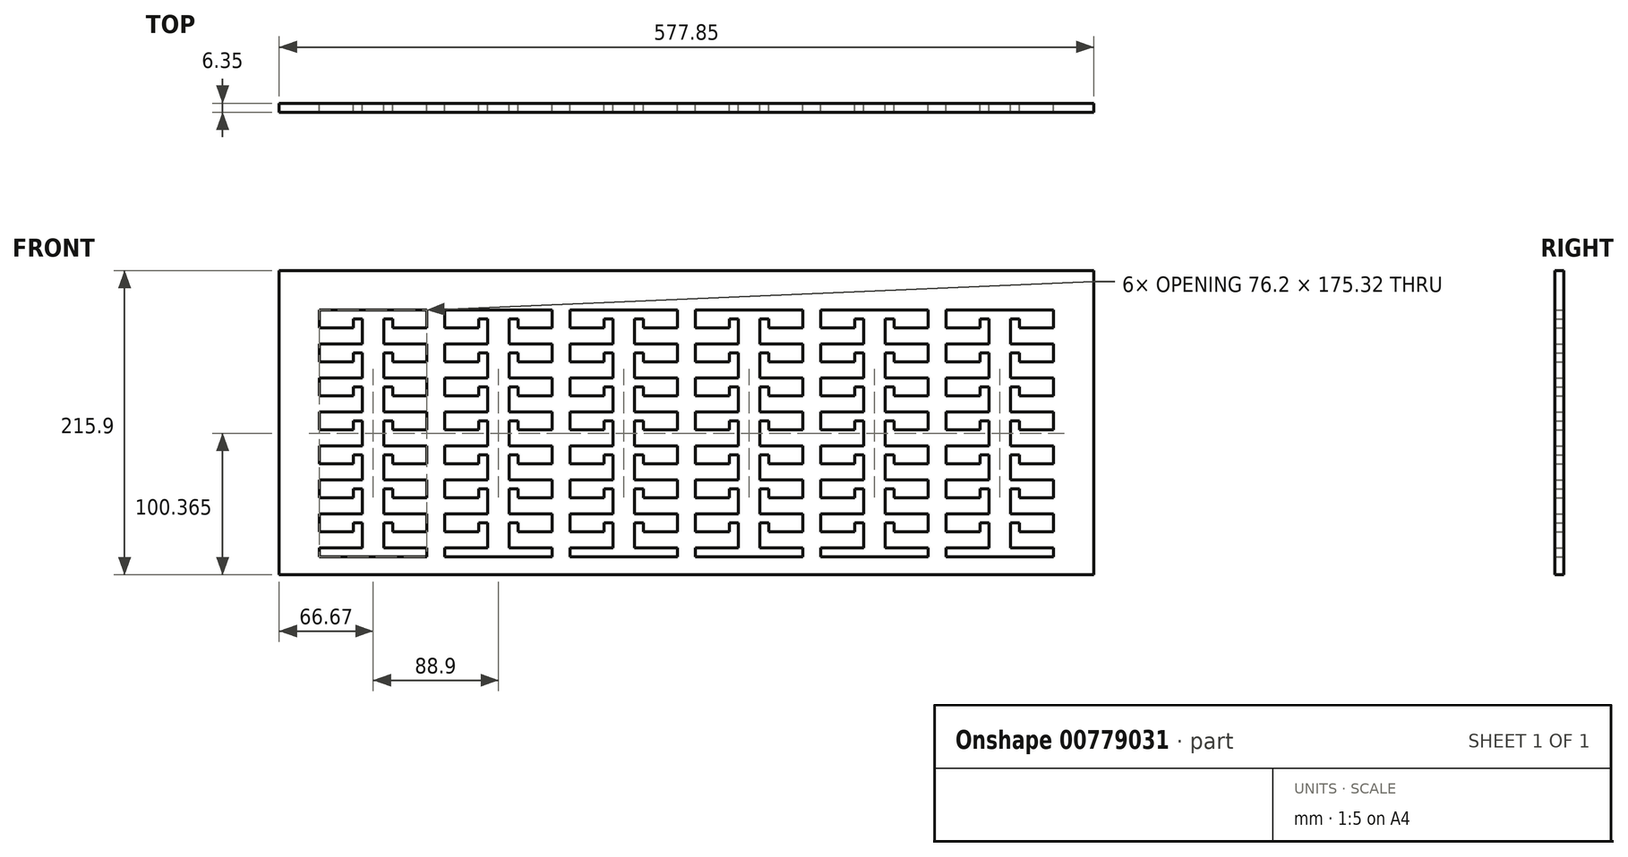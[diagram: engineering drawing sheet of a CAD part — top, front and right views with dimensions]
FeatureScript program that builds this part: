
annotation { "Feature Type Name" : "Feature", "Feature Type Description" : "" }
export const myFeature = defineFeature(function(context is Context, id is Id, definition is map)
    precondition{}
    {
        {
            var Q0;
            Q0=qCreatedBy(makeId("Front.planeOp"),FACE);
            var sketch = newSketch(context, id + "F0", { "sketchPlane" : qUnion([Q0])});
            skLineSegment(sketch, "E0", {"start": v(-97.96, -49.5) * mm, "end": v(-67.48, -49.5) * mm});
            skLineSegment(sketch, "E1", {"start": v(-67.48, -49.5) * mm, "end": v(-67.48, -31.72) * mm});
            skLineSegment(sketch, "E2", {"start": v(-67.48, -31.72) * mm, "end": v(-73.83, -31.72) * mm});
            skLineSegment(sketch, "E3", {"start": v(-73.83, -31.72) * mm, "end": v(-73.83, -38.07) * mm});
            skLineSegment(sketch, "E4", {"start": v(-73.83, -38.07) * mm, "end": v(-97.96, -38.07) * mm});
            skLineSegment(sketch, "E5", {"start": v(-97.96, -38.07) * mm, "end": v(-97.96, -25.37) * mm});
            skLineSegment(sketch, "E6", {"start": v(-97.96, -25.37) * mm, "end": v(-67.48, -25.37) * mm});
            skLineSegment(sketch, "E7", {"start": v(-67.48, -25.37) * mm, "end": v(-67.48, -7.6) * mm});
            skLineSegment(sketch, "E8", {"start": v(-67.48, -7.6) * mm, "end": v(-73.83, -7.6) * mm});
            skLineSegment(sketch, "E9", {"start": v(-73.83, -7.6) * mm, "end": v(-73.83, -13.94) * mm});
            skLineSegment(sketch, "E10", {"start": v(-73.83, -13.94) * mm, "end": v(-97.96, -13.94) * mm});
            skLineSegment(sketch, "E11", {"start": v(-97.96, -13.94) * mm, "end": v(-97.96, -1.24) * mm});
            skLineSegment(sketch, "E12", {"start": v(-97.96, -1.24) * mm, "end": v(-67.48, -1.24) * mm});
            skLineSegment(sketch, "E13", {"start": v(-67.48, -1.24) * mm, "end": v(-67.48, 16.54) * mm});
            skLineSegment(sketch, "E14", {"start": v(-67.48, 16.54) * mm, "end": v(-73.83, 16.54) * mm});
            skLineSegment(sketch, "E15", {"start": v(-73.83, 16.54) * mm, "end": v(-73.83, 10.19) * mm});
            skLineSegment(sketch, "E16", {"start": v(-73.83, 10.19) * mm, "end": v(-97.96, 10.19) * mm});
            skLineSegment(sketch, "E17", {"start": v(-97.96, 10.19) * mm, "end": v(-97.96, 22.89) * mm});
            skLineSegment(sketch, "E18", {"start": v(-97.96, 22.89) * mm, "end": v(-67.48, 22.89) * mm});
            skLineSegment(sketch, "E19", {"start": v(-67.48, 22.89) * mm, "end": v(-67.48, 40.67) * mm});
            skLineSegment(sketch, "E20", {"start": v(-67.48, 40.67) * mm, "end": v(-73.83, 40.67) * mm});
            skLineSegment(sketch, "E21", {"start": v(-73.83, 40.67) * mm, "end": v(-73.83, 34.32) * mm});
            skLineSegment(sketch, "E22", {"start": v(-73.83, 34.32) * mm, "end": v(-97.96, 34.32) * mm});
            skLineSegment(sketch, "E23", {"start": v(-97.96, 34.32) * mm, "end": v(-97.96, 47.02) * mm});
            skLineSegment(sketch, "E24", {"start": v(-21.76, -80.05) * mm, "end": v(-21.76, -73.63) * mm});
            skLineSegment(sketch, "E25", {"start": v(-21.76, -73.63) * mm, "end": v(-52.24, -73.63) * mm});
            skLineSegment(sketch, "E26", {"start": v(-52.24, -73.63) * mm, "end": v(-52.24, -55.85) * mm});
            skLineSegment(sketch, "E27", {"start": v(-52.24, -55.85) * mm, "end": v(-45.89, -55.85) * mm});
            skLineSegment(sketch, "E28", {"start": v(-45.89, -55.85) * mm, "end": v(-45.89, -62.2) * mm});
            skLineSegment(sketch, "E29", {"start": v(-45.89, -62.2) * mm, "end": v(-21.76, -62.2) * mm});
            skLineSegment(sketch, "E30", {"start": v(-21.76, -62.2) * mm, "end": v(-21.76, -49.5) * mm});
            skLineSegment(sketch, "E31", {"start": v(-21.76, -49.5) * mm, "end": v(-52.24, -49.5) * mm});
            skLineSegment(sketch, "E32", {"start": v(-52.24, -49.5) * mm, "end": v(-52.24, -31.72) * mm});
            skLineSegment(sketch, "E33", {"start": v(-52.24, -31.72) * mm, "end": v(-45.89, -31.72) * mm});
            skLineSegment(sketch, "E34", {"start": v(-45.89, -31.72) * mm, "end": v(-45.89, -38.07) * mm});
            skLineSegment(sketch, "E35", {"start": v(-45.89, -38.07) * mm, "end": v(-21.76, -38.07) * mm});
            skLineSegment(sketch, "E36", {"start": v(-21.76, -38.07) * mm, "end": v(-21.76, -25.37) * mm});
            skLineSegment(sketch, "E37", {"start": v(-21.76, -25.37) * mm, "end": v(-52.24, -25.37) * mm});
            skLineSegment(sketch, "E38", {"start": v(-52.24, -25.37) * mm, "end": v(-52.24, -7.6) * mm});
            skLineSegment(sketch, "E39", {"start": v(-52.24, -7.6) * mm, "end": v(-45.89, -7.6) * mm});
            skLineSegment(sketch, "E40", {"start": v(-45.89, -7.6) * mm, "end": v(-45.89, -13.94) * mm});
            skLineSegment(sketch, "E41", {"start": v(-45.89, -13.94) * mm, "end": v(-21.76, -13.94) * mm});
            skLineSegment(sketch, "E42", {"start": v(-21.76, -13.94) * mm, "end": v(-21.76, -1.24) * mm});
            skLineSegment(sketch, "E43", {"start": v(-21.76, -1.24) * mm, "end": v(-52.24, -1.24) * mm});
            skLineSegment(sketch, "E44", {"start": v(-52.24, -1.24) * mm, "end": v(-52.24, 16.54) * mm});
            skLineSegment(sketch, "E45", {"start": v(-52.24, 16.54) * mm, "end": v(-45.89, 16.54) * mm});
            skLineSegment(sketch, "E46", {"start": v(-45.89, 16.54) * mm, "end": v(-45.89, 10.19) * mm});
            skLineSegment(sketch, "E47", {"start": v(-45.89, 10.19) * mm, "end": v(-21.76, 10.19) * mm});
            skLineSegment(sketch, "E48", {"start": v(-21.76, 10.19) * mm, "end": v(-21.76, 22.89) * mm});
            skLineSegment(sketch, "E49", {"start": v(-21.76, 22.89) * mm, "end": v(-52.24, 22.89) * mm});
            skLineSegment(sketch, "E50", {"start": v(-52.24, 22.89) * mm, "end": v(-52.24, 40.67) * mm});
            skLineSegment(sketch, "E51", {"start": v(-52.24, 40.67) * mm, "end": v(-45.89, 40.67) * mm});
            skLineSegment(sketch, "E52", {"start": v(-45.89, 40.67) * mm, "end": v(-45.89, 34.32) * mm});
            skLineSegment(sketch, "E53", {"start": v(-45.89, 34.32) * mm, "end": v(-21.76, 34.32) * mm});
            skLineSegment(sketch, "E54", {"start": v(-21.76, 34.32) * mm, "end": v(-21.76, 47.02) * mm});
            skLineSegment(sketch, "E55", {"start": v(-67.48, -73.63) * mm, "end": v(-67.48, -55.85) * mm});
            skLineSegment(sketch, "E56", {"start": v(-73.83, -62.2) * mm, "end": v(-73.83, -55.85) * mm});
            skLineSegment(sketch, "E57", {"start": v(-73.83, -55.85) * mm, "end": v(-67.48, -55.85) * mm});
            skLineSegment(sketch, "E58", {"start": v(-67.48, -73.63) * mm, "end": v(-97.96, -73.63) * mm});
            skLineSegment(sketch, "E59", {"start": v(-97.96, -62.2) * mm, "end": v(-97.96, -49.5) * mm});
            skLineSegment(sketch, "E60", {"start": v(-97.96, -73.63) * mm, "end": v(-97.96, -80.05) * mm});
            skLineSegment(sketch, "E61", {"start": v(-97.96, -62.2) * mm, "end": v(-73.83, -62.2) * mm});
            skLineSegment(sketch, "E62", {"start": v(-97.96, -80.05) * mm, "end": v(-21.76, -80.05) * mm});
            skPoint(sketch, "E63", {"position": v(-59.86, -80.05) * mm});
            skLineSegment(sketch, "E64", {"start": v(-186.86, -49.5) * mm, "end": v(-156.38, -49.5) * mm});
            skLineSegment(sketch, "E65", {"start": v(-156.38, -49.5) * mm, "end": v(-156.38, -31.72) * mm});
            skLineSegment(sketch, "E66", {"start": v(-156.38, -31.72) * mm, "end": v(-162.73, -31.72) * mm});
            skLineSegment(sketch, "E67", {"start": v(-162.73, -31.72) * mm, "end": v(-162.73, -38.07) * mm});
            skLineSegment(sketch, "E68", {"start": v(-162.73, -38.07) * mm, "end": v(-186.86, -38.07) * mm});
            skLineSegment(sketch, "E69", {"start": v(-186.86, -38.07) * mm, "end": v(-186.86, -25.37) * mm});
            skLineSegment(sketch, "E70", {"start": v(-186.86, -25.37) * mm, "end": v(-156.38, -25.37) * mm});
            skLineSegment(sketch, "E71", {"start": v(-156.38, -25.37) * mm, "end": v(-156.38, -7.6) * mm});
            skLineSegment(sketch, "E72", {"start": v(-156.38, -7.6) * mm, "end": v(-162.73, -7.6) * mm});
            skLineSegment(sketch, "E73", {"start": v(-162.73, -7.6) * mm, "end": v(-162.73, -13.94) * mm});
            skLineSegment(sketch, "E74", {"start": v(-162.73, -13.94) * mm, "end": v(-186.86, -13.94) * mm});
            skLineSegment(sketch, "E75", {"start": v(-186.86, -13.94) * mm, "end": v(-186.86, -1.24) * mm});
            skLineSegment(sketch, "E76", {"start": v(-186.86, -1.24) * mm, "end": v(-156.38, -1.24) * mm});
            skLineSegment(sketch, "E77", {"start": v(-156.38, -1.24) * mm, "end": v(-156.38, 16.54) * mm});
            skLineSegment(sketch, "E78", {"start": v(-156.38, 16.54) * mm, "end": v(-162.73, 16.54) * mm});
            skLineSegment(sketch, "E79", {"start": v(-162.73, 16.54) * mm, "end": v(-162.73, 10.19) * mm});
            skLineSegment(sketch, "E80", {"start": v(-162.73, 10.19) * mm, "end": v(-186.86, 10.19) * mm});
            skLineSegment(sketch, "E81", {"start": v(-186.86, 10.19) * mm, "end": v(-186.86, 22.89) * mm});
            skLineSegment(sketch, "E82", {"start": v(-186.86, 22.89) * mm, "end": v(-156.38, 22.89) * mm});
            skLineSegment(sketch, "E83", {"start": v(-156.38, 22.89) * mm, "end": v(-156.38, 40.67) * mm});
            skLineSegment(sketch, "E84", {"start": v(-156.38, 40.67) * mm, "end": v(-162.73, 40.67) * mm});
            skLineSegment(sketch, "E85", {"start": v(-162.73, 40.67) * mm, "end": v(-162.73, 34.32) * mm});
            skLineSegment(sketch, "E86", {"start": v(-162.73, 34.32) * mm, "end": v(-186.86, 34.32) * mm});
            skLineSegment(sketch, "E87", {"start": v(-186.86, 34.32) * mm, "end": v(-186.86, 47.02) * mm});
            skLineSegment(sketch, "E88", {"start": v(-110.66, -80.05) * mm, "end": v(-110.66, -73.63) * mm});
            skLineSegment(sketch, "E89", {"start": v(-110.66, -73.63) * mm, "end": v(-141.14, -73.63) * mm});
            skLineSegment(sketch, "E90", {"start": v(-141.14, -73.63) * mm, "end": v(-141.14, -55.85) * mm});
            skLineSegment(sketch, "E91", {"start": v(-141.14, -55.85) * mm, "end": v(-134.79, -55.85) * mm});
            skLineSegment(sketch, "E92", {"start": v(-134.79, -55.85) * mm, "end": v(-134.79, -62.2) * mm});
            skLineSegment(sketch, "E93", {"start": v(-134.79, -62.2) * mm, "end": v(-110.66, -62.2) * mm});
            skLineSegment(sketch, "E94", {"start": v(-110.66, -62.2) * mm, "end": v(-110.66, -49.5) * mm});
            skLineSegment(sketch, "E95", {"start": v(-110.66, -49.5) * mm, "end": v(-141.14, -49.5) * mm});
            skLineSegment(sketch, "E96", {"start": v(-141.14, -49.5) * mm, "end": v(-141.14, -31.72) * mm});
            skLineSegment(sketch, "E97", {"start": v(-141.14, -31.72) * mm, "end": v(-134.79, -31.72) * mm});
            skLineSegment(sketch, "E98", {"start": v(-134.79, -31.72) * mm, "end": v(-134.79, -38.07) * mm});
            skLineSegment(sketch, "E99", {"start": v(-134.79, -38.07) * mm, "end": v(-110.66, -38.07) * mm});
            skLineSegment(sketch, "E100", {"start": v(-110.66, -38.07) * mm, "end": v(-110.66, -25.37) * mm});
            skLineSegment(sketch, "E101", {"start": v(-110.66, -25.37) * mm, "end": v(-141.14, -25.37) * mm});
            skLineSegment(sketch, "E102", {"start": v(-141.14, -25.37) * mm, "end": v(-141.14, -7.6) * mm});
            skLineSegment(sketch, "E103", {"start": v(-141.14, -7.6) * mm, "end": v(-134.79, -7.6) * mm});
            skLineSegment(sketch, "E104", {"start": v(-134.79, -7.6) * mm, "end": v(-134.79, -13.94) * mm});
            skLineSegment(sketch, "E105", {"start": v(-134.79, -13.94) * mm, "end": v(-110.66, -13.94) * mm});
            skLineSegment(sketch, "E106", {"start": v(-110.66, -13.94) * mm, "end": v(-110.66, -1.24) * mm});
            skLineSegment(sketch, "E107", {"start": v(-110.66, -1.24) * mm, "end": v(-141.14, -1.24) * mm});
            skLineSegment(sketch, "E108", {"start": v(-141.14, -1.24) * mm, "end": v(-141.14, 16.54) * mm});
            skLineSegment(sketch, "E109", {"start": v(-141.14, 16.54) * mm, "end": v(-134.79, 16.54) * mm});
            skLineSegment(sketch, "E110", {"start": v(-134.79, 16.54) * mm, "end": v(-134.79, 10.19) * mm});
            skLineSegment(sketch, "E111", {"start": v(-134.79, 10.19) * mm, "end": v(-110.66, 10.19) * mm});
            skLineSegment(sketch, "E112", {"start": v(-110.66, 10.19) * mm, "end": v(-110.66, 22.89) * mm});
            skLineSegment(sketch, "E113", {"start": v(-110.66, 22.89) * mm, "end": v(-141.14, 22.89) * mm});
            skLineSegment(sketch, "E114", {"start": v(-141.14, 22.89) * mm, "end": v(-141.14, 40.67) * mm});
            skLineSegment(sketch, "E115", {"start": v(-141.14, 40.67) * mm, "end": v(-134.79, 40.67) * mm});
            skLineSegment(sketch, "E116", {"start": v(-134.79, 40.67) * mm, "end": v(-134.79, 34.32) * mm});
            skLineSegment(sketch, "E117", {"start": v(-134.79, 34.32) * mm, "end": v(-110.66, 34.32) * mm});
            skLineSegment(sketch, "E118", {"start": v(-110.66, 34.32) * mm, "end": v(-110.66, 47.02) * mm});
            skLineSegment(sketch, "E119", {"start": v(-156.38, -73.63) * mm, "end": v(-156.38, -55.85) * mm});
            skLineSegment(sketch, "E120", {"start": v(-162.73, -62.2) * mm, "end": v(-162.73, -55.85) * mm});
            skLineSegment(sketch, "E121", {"start": v(-162.73, -55.85) * mm, "end": v(-156.38, -55.85) * mm});
            skLineSegment(sketch, "E122", {"start": v(-156.38, -73.63) * mm, "end": v(-186.86, -73.63) * mm});
            skLineSegment(sketch, "E123", {"start": v(-186.86, -62.2) * mm, "end": v(-186.86, -49.5) * mm});
            skLineSegment(sketch, "E124", {"start": v(-186.86, -73.63) * mm, "end": v(-186.86, -80.05) * mm});
            skLineSegment(sketch, "E125", {"start": v(-186.86, -62.2) * mm, "end": v(-162.73, -62.2) * mm});
            skLineSegment(sketch, "E126", {"start": v(-186.86, -80.05) * mm, "end": v(-110.66, -80.05) * mm});
            skPoint(sketch, "E127", {"position": v(-148.76, -80.05) * mm});
            skLineSegment(sketch, "E128", {"start": v(-275.76, -49.5) * mm, "end": v(-245.28, -49.5) * mm});
            skLineSegment(sketch, "E129", {"start": v(-245.28, -49.5) * mm, "end": v(-245.28, -31.72) * mm});
            skLineSegment(sketch, "E130", {"start": v(-245.28, -31.72) * mm, "end": v(-251.63, -31.72) * mm});
            skLineSegment(sketch, "E131", {"start": v(-251.63, -31.72) * mm, "end": v(-251.63, -38.07) * mm});
            skLineSegment(sketch, "E132", {"start": v(-251.63, -38.07) * mm, "end": v(-275.76, -38.07) * mm});
            skLineSegment(sketch, "E133", {"start": v(-275.76, -38.07) * mm, "end": v(-275.76, -25.37) * mm});
            skLineSegment(sketch, "E134", {"start": v(-275.76, -25.37) * mm, "end": v(-245.28, -25.37) * mm});
            skLineSegment(sketch, "E135", {"start": v(-245.28, -25.37) * mm, "end": v(-245.28, -7.6) * mm});
            skLineSegment(sketch, "E136", {"start": v(-245.28, -7.6) * mm, "end": v(-251.63, -7.6) * mm});
            skLineSegment(sketch, "E137", {"start": v(-251.63, -7.6) * mm, "end": v(-251.63, -13.94) * mm});
            skLineSegment(sketch, "E138", {"start": v(-251.63, -13.94) * mm, "end": v(-275.76, -13.94) * mm});
            skLineSegment(sketch, "E139", {"start": v(-275.76, -13.94) * mm, "end": v(-275.76, -1.24) * mm});
            skLineSegment(sketch, "E140", {"start": v(-275.76, -1.24) * mm, "end": v(-245.28, -1.24) * mm});
            skLineSegment(sketch, "E141", {"start": v(-245.28, -1.24) * mm, "end": v(-245.28, 16.54) * mm});
            skLineSegment(sketch, "E142", {"start": v(-245.28, 16.54) * mm, "end": v(-251.63, 16.54) * mm});
            skLineSegment(sketch, "E143", {"start": v(-251.63, 16.54) * mm, "end": v(-251.63, 10.19) * mm});
            skLineSegment(sketch, "E144", {"start": v(-251.63, 10.19) * mm, "end": v(-275.76, 10.19) * mm});
            skLineSegment(sketch, "E145", {"start": v(-275.76, 10.19) * mm, "end": v(-275.76, 22.89) * mm});
            skLineSegment(sketch, "E146", {"start": v(-275.76, 22.89) * mm, "end": v(-245.28, 22.89) * mm});
            skLineSegment(sketch, "E147", {"start": v(-245.28, 22.89) * mm, "end": v(-245.28, 40.67) * mm});
            skLineSegment(sketch, "E148", {"start": v(-245.28, 40.67) * mm, "end": v(-251.63, 40.67) * mm});
            skLineSegment(sketch, "E149", {"start": v(-251.63, 40.67) * mm, "end": v(-251.63, 34.32) * mm});
            skLineSegment(sketch, "E150", {"start": v(-251.63, 34.32) * mm, "end": v(-275.76, 34.32) * mm});
            skLineSegment(sketch, "E151", {"start": v(-275.76, 34.32) * mm, "end": v(-275.76, 47.02) * mm});
            skLineSegment(sketch, "E152", {"start": v(-199.56, -80.05) * mm, "end": v(-199.56, -73.63) * mm});
            skLineSegment(sketch, "E153", {"start": v(-199.56, -73.63) * mm, "end": v(-230.04, -73.63) * mm});
            skLineSegment(sketch, "E154", {"start": v(-230.04, -73.63) * mm, "end": v(-230.04, -55.85) * mm});
            skLineSegment(sketch, "E155", {"start": v(-230.04, -55.85) * mm, "end": v(-223.69, -55.85) * mm});
            skLineSegment(sketch, "E156", {"start": v(-223.69, -55.85) * mm, "end": v(-223.69, -62.2) * mm});
            skLineSegment(sketch, "E157", {"start": v(-223.69, -62.2) * mm, "end": v(-199.56, -62.2) * mm});
            skLineSegment(sketch, "E158", {"start": v(-199.56, -62.2) * mm, "end": v(-199.56, -49.5) * mm});
            skLineSegment(sketch, "E159", {"start": v(-199.56, -49.5) * mm, "end": v(-230.04, -49.5) * mm});
            skLineSegment(sketch, "E160", {"start": v(-230.04, -49.5) * mm, "end": v(-230.04, -31.72) * mm});
            skLineSegment(sketch, "E161", {"start": v(-230.04, -31.72) * mm, "end": v(-223.69, -31.72) * mm});
            skLineSegment(sketch, "E162", {"start": v(-223.69, -31.72) * mm, "end": v(-223.69, -38.07) * mm});
            skLineSegment(sketch, "E163", {"start": v(-223.69, -38.07) * mm, "end": v(-199.56, -38.07) * mm});
            skLineSegment(sketch, "E164", {"start": v(-199.56, -38.07) * mm, "end": v(-199.56, -25.37) * mm});
            skLineSegment(sketch, "E165", {"start": v(-199.56, -25.37) * mm, "end": v(-230.04, -25.37) * mm});
            skLineSegment(sketch, "E166", {"start": v(-230.04, -25.37) * mm, "end": v(-230.04, -7.6) * mm});
            skLineSegment(sketch, "E167", {"start": v(-230.04, -7.6) * mm, "end": v(-223.69, -7.6) * mm});
            skLineSegment(sketch, "E168", {"start": v(-223.69, -7.6) * mm, "end": v(-223.69, -13.94) * mm});
            skLineSegment(sketch, "E169", {"start": v(-223.69, -13.94) * mm, "end": v(-199.56, -13.94) * mm});
            skLineSegment(sketch, "E170", {"start": v(-199.56, -13.94) * mm, "end": v(-199.56, -1.24) * mm});
            skLineSegment(sketch, "E171", {"start": v(-199.56, -1.24) * mm, "end": v(-230.04, -1.24) * mm});
            skLineSegment(sketch, "E172", {"start": v(-230.04, -1.24) * mm, "end": v(-230.04, 16.54) * mm});
            skLineSegment(sketch, "E173", {"start": v(-230.04, 16.54) * mm, "end": v(-223.69, 16.54) * mm});
            skLineSegment(sketch, "E174", {"start": v(-223.69, 16.54) * mm, "end": v(-223.69, 10.19) * mm});
            skLineSegment(sketch, "E175", {"start": v(-223.69, 10.19) * mm, "end": v(-199.56, 10.19) * mm});
            skLineSegment(sketch, "E176", {"start": v(-199.56, 10.19) * mm, "end": v(-199.56, 22.89) * mm});
            skLineSegment(sketch, "E177", {"start": v(-199.56, 22.89) * mm, "end": v(-230.04, 22.89) * mm});
            skLineSegment(sketch, "E178", {"start": v(-230.04, 22.89) * mm, "end": v(-230.04, 40.67) * mm});
            skLineSegment(sketch, "E179", {"start": v(-230.04, 40.67) * mm, "end": v(-223.69, 40.67) * mm});
            skLineSegment(sketch, "E180", {"start": v(-223.69, 40.67) * mm, "end": v(-223.69, 34.32) * mm});
            skLineSegment(sketch, "E181", {"start": v(-223.69, 34.32) * mm, "end": v(-199.56, 34.32) * mm});
            skLineSegment(sketch, "E182", {"start": v(-199.56, 34.32) * mm, "end": v(-199.56, 47.02) * mm});
            skLineSegment(sketch, "E183", {"start": v(-245.28, -73.63) * mm, "end": v(-245.28, -55.85) * mm});
            skLineSegment(sketch, "E184", {"start": v(-251.63, -62.2) * mm, "end": v(-251.63, -55.85) * mm});
            skLineSegment(sketch, "E185", {"start": v(-251.63, -55.85) * mm, "end": v(-245.28, -55.85) * mm});
            skLineSegment(sketch, "E186", {"start": v(-245.28, -73.63) * mm, "end": v(-275.76, -73.63) * mm});
            skLineSegment(sketch, "E187", {"start": v(-275.76, -62.2) * mm, "end": v(-275.76, -49.5) * mm});
            skLineSegment(sketch, "E188", {"start": v(-275.76, -73.63) * mm, "end": v(-275.76, -80.05) * mm});
            skLineSegment(sketch, "E189", {"start": v(-275.76, -62.2) * mm, "end": v(-251.63, -62.2) * mm});
            skLineSegment(sketch, "E190", {"start": v(-275.76, -80.05) * mm, "end": v(-199.56, -80.05) * mm});
            skPoint(sketch, "E191", {"position": v(-237.66, -80.05) * mm});
            skLineSegment(sketch, "E192", {"start": v(-364.66, -49.5) * mm, "end": v(-334.18, -49.5) * mm});
            skLineSegment(sketch, "E193", {"start": v(-334.18, -49.5) * mm, "end": v(-334.18, -31.72) * mm});
            skLineSegment(sketch, "E194", {"start": v(-334.18, -31.72) * mm, "end": v(-340.53, -31.72) * mm});
            skLineSegment(sketch, "E195", {"start": v(-340.53, -31.72) * mm, "end": v(-340.53, -38.07) * mm});
            skLineSegment(sketch, "E196", {"start": v(-340.53, -38.07) * mm, "end": v(-364.66, -38.07) * mm});
            skLineSegment(sketch, "E197", {"start": v(-364.66, -38.07) * mm, "end": v(-364.66, -25.37) * mm});
            skLineSegment(sketch, "E198", {"start": v(-364.66, -25.37) * mm, "end": v(-334.18, -25.37) * mm});
            skLineSegment(sketch, "E199", {"start": v(-334.18, -25.37) * mm, "end": v(-334.18, -7.6) * mm});
            skLineSegment(sketch, "E200", {"start": v(-334.18, -7.6) * mm, "end": v(-340.53, -7.6) * mm});
            skLineSegment(sketch, "E201", {"start": v(-340.53, -7.6) * mm, "end": v(-340.53, -13.94) * mm});
            skLineSegment(sketch, "E202", {"start": v(-340.53, -13.94) * mm, "end": v(-364.66, -13.94) * mm});
            skLineSegment(sketch, "E203", {"start": v(-364.66, -13.94) * mm, "end": v(-364.66, -1.24) * mm});
            skLineSegment(sketch, "E204", {"start": v(-364.66, -1.24) * mm, "end": v(-334.18, -1.24) * mm});
            skLineSegment(sketch, "E205", {"start": v(-334.18, -1.24) * mm, "end": v(-334.18, 16.54) * mm});
            skLineSegment(sketch, "E206", {"start": v(-334.18, 16.54) * mm, "end": v(-340.53, 16.54) * mm});
            skLineSegment(sketch, "E207", {"start": v(-340.53, 16.54) * mm, "end": v(-340.53, 10.19) * mm});
            skLineSegment(sketch, "E208", {"start": v(-340.53, 10.19) * mm, "end": v(-364.66, 10.19) * mm});
            skLineSegment(sketch, "E209", {"start": v(-364.66, 10.19) * mm, "end": v(-364.66, 22.89) * mm});
            skLineSegment(sketch, "E210", {"start": v(-364.66, 22.89) * mm, "end": v(-334.18, 22.89) * mm});
            skLineSegment(sketch, "E211", {"start": v(-334.18, 22.89) * mm, "end": v(-334.18, 40.67) * mm});
            skLineSegment(sketch, "E212", {"start": v(-334.18, 40.67) * mm, "end": v(-340.53, 40.67) * mm});
            skLineSegment(sketch, "E213", {"start": v(-340.53, 40.67) * mm, "end": v(-340.53, 34.32) * mm});
            skLineSegment(sketch, "E214", {"start": v(-340.53, 34.32) * mm, "end": v(-364.66, 34.32) * mm});
            skLineSegment(sketch, "E215", {"start": v(-364.66, 34.32) * mm, "end": v(-364.66, 47.02) * mm});
            skLineSegment(sketch, "E216", {"start": v(-288.46, -80.05) * mm, "end": v(-288.46, -73.63) * mm});
            skLineSegment(sketch, "E217", {"start": v(-288.46, -73.63) * mm, "end": v(-318.94, -73.63) * mm});
            skLineSegment(sketch, "E218", {"start": v(-318.94, -73.63) * mm, "end": v(-318.94, -55.85) * mm});
            skLineSegment(sketch, "E219", {"start": v(-318.94, -55.85) * mm, "end": v(-312.59, -55.85) * mm});
            skLineSegment(sketch, "E220", {"start": v(-312.59, -55.85) * mm, "end": v(-312.59, -62.2) * mm});
            skLineSegment(sketch, "E221", {"start": v(-312.59, -62.2) * mm, "end": v(-288.46, -62.2) * mm});
            skLineSegment(sketch, "E222", {"start": v(-288.46, -62.2) * mm, "end": v(-288.46, -49.5) * mm});
            skLineSegment(sketch, "E223", {"start": v(-288.46, -49.5) * mm, "end": v(-318.94, -49.5) * mm});
            skLineSegment(sketch, "E224", {"start": v(-318.94, -49.5) * mm, "end": v(-318.94, -31.72) * mm});
            skLineSegment(sketch, "E225", {"start": v(-318.94, -31.72) * mm, "end": v(-312.59, -31.72) * mm});
            skLineSegment(sketch, "E226", {"start": v(-312.59, -31.72) * mm, "end": v(-312.59, -38.07) * mm});
            skLineSegment(sketch, "E227", {"start": v(-312.59, -38.07) * mm, "end": v(-288.46, -38.07) * mm});
            skLineSegment(sketch, "E228", {"start": v(-288.46, -38.07) * mm, "end": v(-288.46, -25.37) * mm});
            skLineSegment(sketch, "E229", {"start": v(-288.46, -25.37) * mm, "end": v(-318.94, -25.37) * mm});
            skLineSegment(sketch, "E230", {"start": v(-318.94, -25.37) * mm, "end": v(-318.94, -7.6) * mm});
            skLineSegment(sketch, "E231", {"start": v(-318.94, -7.6) * mm, "end": v(-312.59, -7.6) * mm});
            skLineSegment(sketch, "E232", {"start": v(-312.59, -7.6) * mm, "end": v(-312.59, -13.94) * mm});
            skLineSegment(sketch, "E233", {"start": v(-312.59, -13.94) * mm, "end": v(-288.46, -13.94) * mm});
            skLineSegment(sketch, "E234", {"start": v(-288.46, -13.94) * mm, "end": v(-288.46, -1.24) * mm});
            skLineSegment(sketch, "E235", {"start": v(-288.46, -1.24) * mm, "end": v(-318.94, -1.24) * mm});
            skLineSegment(sketch, "E236", {"start": v(-318.94, -1.24) * mm, "end": v(-318.94, 16.54) * mm});
            skLineSegment(sketch, "E237", {"start": v(-318.94, 16.54) * mm, "end": v(-312.59, 16.54) * mm});
            skLineSegment(sketch, "E238", {"start": v(-312.59, 16.54) * mm, "end": v(-312.59, 10.19) * mm});
            skLineSegment(sketch, "E239", {"start": v(-312.59, 10.19) * mm, "end": v(-288.46, 10.19) * mm});
            skLineSegment(sketch, "E240", {"start": v(-288.46, 10.19) * mm, "end": v(-288.46, 22.89) * mm});
            skLineSegment(sketch, "E241", {"start": v(-288.46, 22.89) * mm, "end": v(-318.94, 22.89) * mm});
            skLineSegment(sketch, "E242", {"start": v(-318.94, 22.89) * mm, "end": v(-318.94, 40.67) * mm});
            skLineSegment(sketch, "E243", {"start": v(-318.94, 40.67) * mm, "end": v(-312.59, 40.67) * mm});
            skLineSegment(sketch, "E244", {"start": v(-312.59, 40.67) * mm, "end": v(-312.59, 34.32) * mm});
            skLineSegment(sketch, "E245", {"start": v(-312.59, 34.32) * mm, "end": v(-288.46, 34.32) * mm});
            skLineSegment(sketch, "E246", {"start": v(-288.46, 34.32) * mm, "end": v(-288.46, 47.02) * mm});
            skLineSegment(sketch, "E247", {"start": v(-334.18, -73.63) * mm, "end": v(-334.18, -55.85) * mm});
            skLineSegment(sketch, "E248", {"start": v(-340.53, -62.2) * mm, "end": v(-340.53, -55.85) * mm});
            skLineSegment(sketch, "E249", {"start": v(-340.53, -55.85) * mm, "end": v(-334.18, -55.85) * mm});
            skLineSegment(sketch, "E250", {"start": v(-334.18, -73.63) * mm, "end": v(-364.66, -73.63) * mm});
            skLineSegment(sketch, "E251", {"start": v(-364.66, -62.2) * mm, "end": v(-364.66, -49.5) * mm});
            skLineSegment(sketch, "E252", {"start": v(-364.66, -73.63) * mm, "end": v(-364.66, -80.05) * mm});
            skLineSegment(sketch, "E253", {"start": v(-364.66, -62.2) * mm, "end": v(-340.53, -62.2) * mm});
            skLineSegment(sketch, "E254", {"start": v(-364.66, -80.05) * mm, "end": v(-288.46, -80.05) * mm});
            skPoint(sketch, "E255", {"position": v(-326.56, -80.05) * mm});
            skLineSegment(sketch, "E256.bottom", {"start": v(6.82, 123.15) * mm, "end": v(-571.03, 123.15) * mm});
            skLineSegment(sketch, "E256.top", {"start": v(6.82, -92.75) * mm, "end": v(-571.03, -92.75) * mm});
            skLineSegment(sketch, "E256.left", {"start": v(6.82, 123.15) * mm, "end": v(6.82, -92.75) * mm});
            skLineSegment(sketch, "E256.right", {"start": v(-571.03, 123.15) * mm, "end": v(-571.03, -92.75) * mm});
            skPoint(sketch, "E257", {"position": v(-282.1, 123.15) * mm});
            skLineSegment(sketch, "E258", {"start": v(-453.56, -49.5) * mm, "end": v(-423.08, -49.5) * mm});
            skLineSegment(sketch, "E259", {"start": v(-423.08, -49.5) * mm, "end": v(-423.08, -31.72) * mm});
            skLineSegment(sketch, "E260", {"start": v(-423.08, -31.72) * mm, "end": v(-429.43, -31.72) * mm});
            skLineSegment(sketch, "E261", {"start": v(-429.43, -31.72) * mm, "end": v(-429.43, -38.07) * mm});
            skLineSegment(sketch, "E262", {"start": v(-429.43, -38.07) * mm, "end": v(-453.56, -38.07) * mm});
            skLineSegment(sketch, "E263", {"start": v(-453.56, -38.07) * mm, "end": v(-453.56, -25.37) * mm});
            skLineSegment(sketch, "E264", {"start": v(-453.56, -25.37) * mm, "end": v(-423.08, -25.37) * mm});
            skLineSegment(sketch, "E265", {"start": v(-423.08, -25.37) * mm, "end": v(-423.08, -7.6) * mm});
            skLineSegment(sketch, "E266", {"start": v(-423.08, -7.6) * mm, "end": v(-429.43, -7.6) * mm});
            skLineSegment(sketch, "E267", {"start": v(-429.43, -7.6) * mm, "end": v(-429.43, -13.94) * mm});
            skLineSegment(sketch, "E268", {"start": v(-429.43, -13.94) * mm, "end": v(-453.56, -13.94) * mm});
            skLineSegment(sketch, "E269", {"start": v(-453.56, -13.94) * mm, "end": v(-453.56, -1.24) * mm});
            skLineSegment(sketch, "E270", {"start": v(-453.56, -1.24) * mm, "end": v(-423.08, -1.24) * mm});
            skLineSegment(sketch, "E271", {"start": v(-423.08, -1.24) * mm, "end": v(-423.08, 16.54) * mm});
            skLineSegment(sketch, "E272", {"start": v(-423.08, 16.54) * mm, "end": v(-429.43, 16.54) * mm});
            skLineSegment(sketch, "E273", {"start": v(-429.43, 16.54) * mm, "end": v(-429.43, 10.19) * mm});
            skLineSegment(sketch, "E274", {"start": v(-429.43, 10.19) * mm, "end": v(-453.56, 10.19) * mm});
            skLineSegment(sketch, "E275", {"start": v(-453.56, 10.19) * mm, "end": v(-453.56, 22.89) * mm});
            skLineSegment(sketch, "E276", {"start": v(-453.56, 22.89) * mm, "end": v(-423.08, 22.89) * mm});
            skLineSegment(sketch, "E277", {"start": v(-423.08, 22.89) * mm, "end": v(-423.08, 40.67) * mm});
            skLineSegment(sketch, "E278", {"start": v(-423.08, 40.67) * mm, "end": v(-429.43, 40.67) * mm});
            skLineSegment(sketch, "E279", {"start": v(-429.43, 40.67) * mm, "end": v(-429.43, 34.32) * mm});
            skLineSegment(sketch, "E280", {"start": v(-429.43, 34.32) * mm, "end": v(-453.56, 34.32) * mm});
            skLineSegment(sketch, "E281", {"start": v(-453.56, 34.32) * mm, "end": v(-453.56, 47.02) * mm});
            skLineSegment(sketch, "E282", {"start": v(-377.36, -80.05) * mm, "end": v(-377.36, -73.63) * mm});
            skLineSegment(sketch, "E283", {"start": v(-377.36, -73.63) * mm, "end": v(-407.84, -73.63) * mm});
            skLineSegment(sketch, "E284", {"start": v(-407.84, -73.63) * mm, "end": v(-407.84, -55.85) * mm});
            skLineSegment(sketch, "E285", {"start": v(-407.84, -55.85) * mm, "end": v(-401.49, -55.85) * mm});
            skLineSegment(sketch, "E286", {"start": v(-401.49, -55.85) * mm, "end": v(-401.49, -62.2) * mm});
            skLineSegment(sketch, "E287", {"start": v(-401.49, -62.2) * mm, "end": v(-377.36, -62.2) * mm});
            skLineSegment(sketch, "E288", {"start": v(-377.36, -62.2) * mm, "end": v(-377.36, -49.5) * mm});
            skLineSegment(sketch, "E289", {"start": v(-377.36, -49.5) * mm, "end": v(-407.84, -49.5) * mm});
            skLineSegment(sketch, "E290", {"start": v(-407.84, -49.5) * mm, "end": v(-407.84, -31.72) * mm});
            skLineSegment(sketch, "E291", {"start": v(-407.84, -31.72) * mm, "end": v(-401.49, -31.72) * mm});
            skLineSegment(sketch, "E292", {"start": v(-401.49, -31.72) * mm, "end": v(-401.49, -38.07) * mm});
            skLineSegment(sketch, "E293", {"start": v(-401.49, -38.07) * mm, "end": v(-377.36, -38.07) * mm});
            skLineSegment(sketch, "E294", {"start": v(-377.36, -38.07) * mm, "end": v(-377.36, -25.37) * mm});
            skLineSegment(sketch, "E295", {"start": v(-377.36, -25.37) * mm, "end": v(-407.84, -25.37) * mm});
            skLineSegment(sketch, "E296", {"start": v(-407.84, -25.37) * mm, "end": v(-407.84, -7.6) * mm});
            skLineSegment(sketch, "E297", {"start": v(-407.84, -7.6) * mm, "end": v(-401.49, -7.6) * mm});
            skLineSegment(sketch, "E298", {"start": v(-401.49, -7.6) * mm, "end": v(-401.49, -13.94) * mm});
            skLineSegment(sketch, "E299", {"start": v(-401.49, -13.94) * mm, "end": v(-377.36, -13.94) * mm});
            skLineSegment(sketch, "E300", {"start": v(-377.36, -13.94) * mm, "end": v(-377.36, -1.24) * mm});
            skLineSegment(sketch, "E301", {"start": v(-377.36, -1.24) * mm, "end": v(-407.84, -1.24) * mm});
            skLineSegment(sketch, "E302", {"start": v(-407.84, -1.24) * mm, "end": v(-407.84, 16.54) * mm});
            skLineSegment(sketch, "E303", {"start": v(-407.84, 16.54) * mm, "end": v(-401.49, 16.54) * mm});
            skLineSegment(sketch, "E304", {"start": v(-401.49, 16.54) * mm, "end": v(-401.49, 10.19) * mm});
            skLineSegment(sketch, "E305", {"start": v(-401.49, 10.19) * mm, "end": v(-377.36, 10.19) * mm});
            skLineSegment(sketch, "E306", {"start": v(-377.36, 10.19) * mm, "end": v(-377.36, 22.89) * mm});
            skLineSegment(sketch, "E307", {"start": v(-377.36, 22.89) * mm, "end": v(-407.84, 22.89) * mm});
            skLineSegment(sketch, "E308", {"start": v(-407.84, 22.89) * mm, "end": v(-407.84, 40.67) * mm});
            skLineSegment(sketch, "E309", {"start": v(-407.84, 40.67) * mm, "end": v(-401.49, 40.67) * mm});
            skLineSegment(sketch, "E310", {"start": v(-401.49, 40.67) * mm, "end": v(-401.49, 34.32) * mm});
            skLineSegment(sketch, "E311", {"start": v(-401.49, 34.32) * mm, "end": v(-377.36, 34.32) * mm});
            skLineSegment(sketch, "E312", {"start": v(-377.36, 34.32) * mm, "end": v(-377.36, 47.02) * mm});
            skLineSegment(sketch, "E313", {"start": v(-423.08, -73.63) * mm, "end": v(-423.08, -55.85) * mm});
            skLineSegment(sketch, "E314", {"start": v(-429.43, -62.2) * mm, "end": v(-429.43, -55.85) * mm});
            skLineSegment(sketch, "E315", {"start": v(-429.43, -55.85) * mm, "end": v(-423.08, -55.85) * mm});
            skLineSegment(sketch, "E316", {"start": v(-423.08, -73.63) * mm, "end": v(-453.56, -73.63) * mm});
            skLineSegment(sketch, "E317", {"start": v(-453.56, -62.2) * mm, "end": v(-453.56, -49.5) * mm});
            skLineSegment(sketch, "E318", {"start": v(-453.56, -73.63) * mm, "end": v(-453.56, -80.05) * mm});
            skLineSegment(sketch, "E319", {"start": v(-453.56, -62.2) * mm, "end": v(-429.43, -62.2) * mm});
            skLineSegment(sketch, "E320", {"start": v(-453.56, -80.05) * mm, "end": v(-377.36, -80.05) * mm});
            skPoint(sketch, "E321", {"position": v(-415.46, -80.05) * mm});
            skLineSegment(sketch, "E322", {"start": v(-542.46, -49.5) * mm, "end": v(-511.98, -49.5) * mm});
            skLineSegment(sketch, "E323", {"start": v(-511.98, -49.5) * mm, "end": v(-511.98, -31.72) * mm});
            skLineSegment(sketch, "E324", {"start": v(-511.98, -31.72) * mm, "end": v(-518.33, -31.72) * mm});
            skLineSegment(sketch, "E325", {"start": v(-518.33, -31.72) * mm, "end": v(-518.33, -38.07) * mm});
            skLineSegment(sketch, "E326", {"start": v(-518.33, -38.07) * mm, "end": v(-542.46, -38.07) * mm});
            skLineSegment(sketch, "E327", {"start": v(-542.46, -38.07) * mm, "end": v(-542.46, -25.37) * mm});
            skLineSegment(sketch, "E328", {"start": v(-542.46, -25.37) * mm, "end": v(-511.98, -25.37) * mm});
            skLineSegment(sketch, "E329", {"start": v(-511.98, -25.37) * mm, "end": v(-511.98, -7.6) * mm});
            skLineSegment(sketch, "E330", {"start": v(-511.98, -7.6) * mm, "end": v(-518.33, -7.6) * mm});
            skLineSegment(sketch, "E331", {"start": v(-518.33, -7.6) * mm, "end": v(-518.33, -13.94) * mm});
            skLineSegment(sketch, "E332", {"start": v(-518.33, -13.94) * mm, "end": v(-542.46, -13.94) * mm});
            skLineSegment(sketch, "E333", {"start": v(-542.46, -13.94) * mm, "end": v(-542.46, -1.24) * mm});
            skLineSegment(sketch, "E334", {"start": v(-542.46, -1.24) * mm, "end": v(-511.98, -1.24) * mm});
            skLineSegment(sketch, "E335", {"start": v(-511.98, -1.24) * mm, "end": v(-511.98, 16.54) * mm});
            skLineSegment(sketch, "E336", {"start": v(-511.98, 16.54) * mm, "end": v(-518.33, 16.54) * mm});
            skLineSegment(sketch, "E337", {"start": v(-518.33, 16.54) * mm, "end": v(-518.33, 10.19) * mm});
            skLineSegment(sketch, "E338", {"start": v(-518.33, 10.19) * mm, "end": v(-542.46, 10.19) * mm});
            skLineSegment(sketch, "E339", {"start": v(-542.46, 10.19) * mm, "end": v(-542.46, 22.89) * mm});
            skLineSegment(sketch, "E340", {"start": v(-542.46, 22.89) * mm, "end": v(-511.98, 22.89) * mm});
            skLineSegment(sketch, "E341", {"start": v(-511.98, 22.89) * mm, "end": v(-511.98, 40.67) * mm});
            skLineSegment(sketch, "E342", {"start": v(-511.98, 40.67) * mm, "end": v(-518.33, 40.67) * mm});
            skLineSegment(sketch, "E343", {"start": v(-518.33, 40.67) * mm, "end": v(-518.33, 34.32) * mm});
            skLineSegment(sketch, "E344", {"start": v(-518.33, 34.32) * mm, "end": v(-542.46, 34.32) * mm});
            skLineSegment(sketch, "E345", {"start": v(-542.46, 34.32) * mm, "end": v(-542.46, 47.02) * mm});
            skLineSegment(sketch, "E346", {"start": v(-466.26, -80.05) * mm, "end": v(-466.26, -73.63) * mm});
            skLineSegment(sketch, "E347", {"start": v(-466.26, -73.63) * mm, "end": v(-496.74, -73.63) * mm});
            skLineSegment(sketch, "E348", {"start": v(-496.74, -73.63) * mm, "end": v(-496.74, -55.85) * mm});
            skLineSegment(sketch, "E349", {"start": v(-496.74, -55.85) * mm, "end": v(-490.39, -55.85) * mm});
            skLineSegment(sketch, "E350", {"start": v(-490.39, -55.85) * mm, "end": v(-490.39, -62.2) * mm});
            skLineSegment(sketch, "E351", {"start": v(-490.39, -62.2) * mm, "end": v(-466.26, -62.2) * mm});
            skLineSegment(sketch, "E352", {"start": v(-466.26, -62.2) * mm, "end": v(-466.26, -49.5) * mm});
            skLineSegment(sketch, "E353", {"start": v(-466.26, -49.5) * mm, "end": v(-496.74, -49.5) * mm});
            skLineSegment(sketch, "E354", {"start": v(-496.74, -49.5) * mm, "end": v(-496.74, -31.72) * mm});
            skLineSegment(sketch, "E355", {"start": v(-496.74, -31.72) * mm, "end": v(-490.39, -31.72) * mm});
            skLineSegment(sketch, "E356", {"start": v(-490.39, -31.72) * mm, "end": v(-490.39, -38.07) * mm});
            skLineSegment(sketch, "E357", {"start": v(-490.39, -38.07) * mm, "end": v(-466.26, -38.07) * mm});
            skLineSegment(sketch, "E358", {"start": v(-466.26, -38.07) * mm, "end": v(-466.26, -25.37) * mm});
            skLineSegment(sketch, "E359", {"start": v(-466.26, -25.37) * mm, "end": v(-496.74, -25.37) * mm});
            skLineSegment(sketch, "E360", {"start": v(-496.74, -25.37) * mm, "end": v(-496.74, -7.6) * mm});
            skLineSegment(sketch, "E361", {"start": v(-496.74, -7.6) * mm, "end": v(-490.39, -7.6) * mm});
            skLineSegment(sketch, "E362", {"start": v(-490.39, -7.6) * mm, "end": v(-490.39, -13.94) * mm});
            skLineSegment(sketch, "E363", {"start": v(-490.39, -13.94) * mm, "end": v(-466.26, -13.94) * mm});
            skLineSegment(sketch, "E364", {"start": v(-466.26, -13.94) * mm, "end": v(-466.26, -1.24) * mm});
            skLineSegment(sketch, "E365", {"start": v(-466.26, -1.24) * mm, "end": v(-496.74, -1.24) * mm});
            skLineSegment(sketch, "E366", {"start": v(-496.74, -1.24) * mm, "end": v(-496.74, 16.54) * mm});
            skLineSegment(sketch, "E367", {"start": v(-496.74, 16.54) * mm, "end": v(-490.39, 16.54) * mm});
            skLineSegment(sketch, "E368", {"start": v(-490.39, 16.54) * mm, "end": v(-490.39, 10.19) * mm});
            skLineSegment(sketch, "E369", {"start": v(-490.39, 10.19) * mm, "end": v(-466.26, 10.19) * mm});
            skLineSegment(sketch, "E370", {"start": v(-466.26, 10.19) * mm, "end": v(-466.26, 22.89) * mm});
            skLineSegment(sketch, "E371", {"start": v(-466.26, 22.89) * mm, "end": v(-496.74, 22.89) * mm});
            skLineSegment(sketch, "E372", {"start": v(-496.74, 22.89) * mm, "end": v(-496.74, 40.67) * mm});
            skLineSegment(sketch, "E373", {"start": v(-496.74, 40.67) * mm, "end": v(-490.39, 40.67) * mm});
            skLineSegment(sketch, "E374", {"start": v(-490.39, 40.67) * mm, "end": v(-490.39, 34.32) * mm});
            skLineSegment(sketch, "E375", {"start": v(-490.39, 34.32) * mm, "end": v(-466.26, 34.32) * mm});
            skLineSegment(sketch, "E376", {"start": v(-466.26, 34.32) * mm, "end": v(-466.26, 47.02) * mm});
            skLineSegment(sketch, "E377", {"start": v(-511.98, -73.63) * mm, "end": v(-511.98, -55.85) * mm});
            skLineSegment(sketch, "E378", {"start": v(-518.33, -62.2) * mm, "end": v(-518.33, -55.85) * mm});
            skLineSegment(sketch, "E379", {"start": v(-518.33, -55.85) * mm, "end": v(-511.98, -55.85) * mm});
            skLineSegment(sketch, "E380", {"start": v(-511.98, -73.63) * mm, "end": v(-542.46, -73.63) * mm});
            skLineSegment(sketch, "E381", {"start": v(-542.46, -62.2) * mm, "end": v(-542.46, -49.5) * mm});
            skLineSegment(sketch, "E382", {"start": v(-542.46, -73.63) * mm, "end": v(-542.46, -80.05) * mm});
            skLineSegment(sketch, "E383", {"start": v(-542.46, -62.2) * mm, "end": v(-518.33, -62.2) * mm});
            skLineSegment(sketch, "E384", {"start": v(-542.46, -80.05) * mm, "end": v(-466.26, -80.05) * mm});
            skPoint(sketch, "E385", {"position": v(-504.36, -80.05) * mm});
            skLineSegment(sketch, "E386", {"start": v(-542.46, 47.02) * mm, "end": v(-511.98, 47.02) * mm});
            skLineSegment(sketch, "E387", {"start": v(-511.98, 47.02) * mm, "end": v(-511.98, 64.8) * mm});
            skLineSegment(sketch, "E388", {"start": v(-511.98, 64.8) * mm, "end": v(-518.33, 64.8) * mm});
            skLineSegment(sketch, "E389", {"start": v(-518.33, 64.8) * mm, "end": v(-518.33, 58.45) * mm});
            skLineSegment(sketch, "E390", {"start": v(-518.33, 58.45) * mm, "end": v(-542.46, 58.45) * mm});
            skLineSegment(sketch, "E391", {"start": v(-542.46, 58.45) * mm, "end": v(-542.46, 71.15) * mm});
            skLineSegment(sketch, "E392", {"start": v(-542.46, 71.15) * mm, "end": v(-511.98, 71.15) * mm});
            skLineSegment(sketch, "E393", {"start": v(-511.98, 88.93) * mm, "end": v(-518.33, 88.93) * mm});
            skLineSegment(sketch, "E394", {"start": v(-518.33, 88.93) * mm, "end": v(-518.33, 82.58) * mm});
            skLineSegment(sketch, "E395", {"start": v(-518.33, 82.58) * mm, "end": v(-542.46, 82.58) * mm});
            skLineSegment(sketch, "E396", {"start": v(-542.46, 82.58) * mm, "end": v(-542.46, 95.28) * mm});
            skLineSegment(sketch, "E397", {"start": v(-466.26, 47.02) * mm, "end": v(-496.74, 47.02) * mm});
            skLineSegment(sketch, "E398", {"start": v(-496.74, 47.02) * mm, "end": v(-496.74, 64.8) * mm});
            skLineSegment(sketch, "E399", {"start": v(-496.74, 64.8) * mm, "end": v(-490.39, 64.8) * mm});
            skLineSegment(sketch, "E400", {"start": v(-490.39, 64.8) * mm, "end": v(-490.39, 58.45) * mm});
            skLineSegment(sketch, "E401", {"start": v(-490.39, 58.45) * mm, "end": v(-466.26, 58.45) * mm});
            skLineSegment(sketch, "E402", {"start": v(-466.26, 58.45) * mm, "end": v(-466.26, 71.15) * mm});
            skLineSegment(sketch, "E403", {"start": v(-466.26, 71.15) * mm, "end": v(-496.74, 71.15) * mm});
            skLineSegment(sketch, "E404", {"start": v(-496.74, 71.15) * mm, "end": v(-496.74, 88.93) * mm});
            skLineSegment(sketch, "E405", {"start": v(-496.74, 88.93) * mm, "end": v(-490.39, 88.93) * mm});
            skLineSegment(sketch, "E406", {"start": v(-490.39, 88.93) * mm, "end": v(-490.39, 82.58) * mm});
            skLineSegment(sketch, "E407", {"start": v(-490.39, 82.58) * mm, "end": v(-466.26, 82.58) * mm});
            skLineSegment(sketch, "E408", {"start": v(-466.26, 82.58) * mm, "end": v(-466.26, 95.28) * mm});
            skLineSegment(sketch, "E409", {"start": v(-511.98, 71.15) * mm, "end": v(-511.98, 88.93) * mm});
            skLineSegment(sketch, "E410", {"start": v(-542.46, 95.28) * mm, "end": v(-466.26, 95.28) * mm});
            skPoint(sketch, "E411", {"position": v(-504.36, 95.28) * mm});
            skLineSegment(sketch, "E412", {"start": v(-453.56, 47.02) * mm, "end": v(-423.08, 47.02) * mm});
            skLineSegment(sketch, "E413", {"start": v(-423.08, 47.02) * mm, "end": v(-423.08, 64.8) * mm});
            skLineSegment(sketch, "E414", {"start": v(-423.08, 64.8) * mm, "end": v(-429.43, 64.8) * mm});
            skLineSegment(sketch, "E415", {"start": v(-429.43, 64.8) * mm, "end": v(-429.43, 58.45) * mm});
            skLineSegment(sketch, "E416", {"start": v(-429.43, 58.45) * mm, "end": v(-453.56, 58.45) * mm});
            skLineSegment(sketch, "E417", {"start": v(-453.56, 58.45) * mm, "end": v(-453.56, 71.15) * mm});
            skLineSegment(sketch, "E418", {"start": v(-453.56, 71.15) * mm, "end": v(-423.08, 71.15) * mm});
            skLineSegment(sketch, "E419", {"start": v(-423.08, 88.93) * mm, "end": v(-429.43, 88.93) * mm});
            skLineSegment(sketch, "E420", {"start": v(-429.43, 88.93) * mm, "end": v(-429.43, 82.58) * mm});
            skLineSegment(sketch, "E421", {"start": v(-429.43, 82.58) * mm, "end": v(-453.56, 82.58) * mm});
            skLineSegment(sketch, "E422", {"start": v(-453.56, 82.58) * mm, "end": v(-453.56, 95.28) * mm});
            skLineSegment(sketch, "E423", {"start": v(-377.36, 47.02) * mm, "end": v(-407.84, 47.02) * mm});
            skLineSegment(sketch, "E424", {"start": v(-407.84, 47.02) * mm, "end": v(-407.84, 64.8) * mm});
            skLineSegment(sketch, "E425", {"start": v(-407.84, 64.8) * mm, "end": v(-401.49, 64.8) * mm});
            skLineSegment(sketch, "E426", {"start": v(-401.49, 64.8) * mm, "end": v(-401.49, 58.45) * mm});
            skLineSegment(sketch, "E427", {"start": v(-401.49, 58.45) * mm, "end": v(-377.36, 58.45) * mm});
            skLineSegment(sketch, "E428", {"start": v(-377.36, 58.45) * mm, "end": v(-377.36, 71.15) * mm});
            skLineSegment(sketch, "E429", {"start": v(-377.36, 71.15) * mm, "end": v(-407.84, 71.15) * mm});
            skLineSegment(sketch, "E430", {"start": v(-407.84, 71.15) * mm, "end": v(-407.84, 88.93) * mm});
            skLineSegment(sketch, "E431", {"start": v(-407.84, 88.93) * mm, "end": v(-401.49, 88.93) * mm});
            skLineSegment(sketch, "E432", {"start": v(-401.49, 88.93) * mm, "end": v(-401.49, 82.58) * mm});
            skLineSegment(sketch, "E433", {"start": v(-401.49, 82.58) * mm, "end": v(-377.36, 82.58) * mm});
            skLineSegment(sketch, "E434", {"start": v(-377.36, 82.58) * mm, "end": v(-377.36, 95.28) * mm});
            skLineSegment(sketch, "E435", {"start": v(-423.08, 71.15) * mm, "end": v(-423.08, 88.93) * mm});
            skLineSegment(sketch, "E436", {"start": v(-453.56, 95.28) * mm, "end": v(-377.36, 95.28) * mm});
            skPoint(sketch, "E437", {"position": v(-415.46, 95.28) * mm});
            skLineSegment(sketch, "E438", {"start": v(-364.66, 47.02) * mm, "end": v(-334.18, 47.02) * mm});
            skLineSegment(sketch, "E439", {"start": v(-334.18, 47.02) * mm, "end": v(-334.18, 64.8) * mm});
            skLineSegment(sketch, "E440", {"start": v(-334.18, 64.8) * mm, "end": v(-340.53, 64.8) * mm});
            skLineSegment(sketch, "E441", {"start": v(-340.53, 64.8) * mm, "end": v(-340.53, 58.45) * mm});
            skLineSegment(sketch, "E442", {"start": v(-340.53, 58.45) * mm, "end": v(-364.66, 58.45) * mm});
            skLineSegment(sketch, "E443", {"start": v(-364.66, 58.45) * mm, "end": v(-364.66, 71.15) * mm});
            skLineSegment(sketch, "E444", {"start": v(-364.66, 71.15) * mm, "end": v(-334.18, 71.15) * mm});
            skLineSegment(sketch, "E445", {"start": v(-334.18, 88.93) * mm, "end": v(-340.53, 88.93) * mm});
            skLineSegment(sketch, "E446", {"start": v(-340.53, 88.93) * mm, "end": v(-340.53, 82.58) * mm});
            skLineSegment(sketch, "E447", {"start": v(-340.53, 82.58) * mm, "end": v(-364.66, 82.58) * mm});
            skLineSegment(sketch, "E448", {"start": v(-364.66, 82.58) * mm, "end": v(-364.66, 95.28) * mm});
            skLineSegment(sketch, "E449", {"start": v(-288.46, 47.02) * mm, "end": v(-318.94, 47.02) * mm});
            skLineSegment(sketch, "E450", {"start": v(-318.94, 47.02) * mm, "end": v(-318.94, 64.8) * mm});
            skLineSegment(sketch, "E451", {"start": v(-318.94, 64.8) * mm, "end": v(-312.59, 64.8) * mm});
            skLineSegment(sketch, "E452", {"start": v(-312.59, 64.8) * mm, "end": v(-312.59, 58.45) * mm});
            skLineSegment(sketch, "E453", {"start": v(-312.59, 58.45) * mm, "end": v(-288.46, 58.45) * mm});
            skLineSegment(sketch, "E454", {"start": v(-288.46, 58.45) * mm, "end": v(-288.46, 71.15) * mm});
            skLineSegment(sketch, "E455", {"start": v(-288.46, 71.15) * mm, "end": v(-318.94, 71.15) * mm});
            skLineSegment(sketch, "E456", {"start": v(-318.94, 71.15) * mm, "end": v(-318.94, 88.93) * mm});
            skLineSegment(sketch, "E457", {"start": v(-318.94, 88.93) * mm, "end": v(-312.59, 88.93) * mm});
            skLineSegment(sketch, "E458", {"start": v(-312.59, 88.93) * mm, "end": v(-312.59, 82.58) * mm});
            skLineSegment(sketch, "E459", {"start": v(-312.59, 82.58) * mm, "end": v(-288.46, 82.58) * mm});
            skLineSegment(sketch, "E460", {"start": v(-288.46, 82.58) * mm, "end": v(-288.46, 95.28) * mm});
            skLineSegment(sketch, "E461", {"start": v(-334.18, 71.15) * mm, "end": v(-334.18, 88.93) * mm});
            skLineSegment(sketch, "E462", {"start": v(-364.66, 95.28) * mm, "end": v(-288.46, 95.28) * mm});
            skPoint(sketch, "E463", {"position": v(-326.56, 95.28) * mm});
            skLineSegment(sketch, "E464", {"start": v(-275.76, 47.02) * mm, "end": v(-245.28, 47.02) * mm});
            skLineSegment(sketch, "E465", {"start": v(-245.28, 47.02) * mm, "end": v(-245.28, 64.8) * mm});
            skLineSegment(sketch, "E466", {"start": v(-245.28, 64.8) * mm, "end": v(-251.63, 64.8) * mm});
            skLineSegment(sketch, "E467", {"start": v(-251.63, 64.8) * mm, "end": v(-251.63, 58.45) * mm});
            skLineSegment(sketch, "E468", {"start": v(-251.63, 58.45) * mm, "end": v(-275.76, 58.45) * mm});
            skLineSegment(sketch, "E469", {"start": v(-275.76, 58.45) * mm, "end": v(-275.76, 71.15) * mm});
            skLineSegment(sketch, "E470", {"start": v(-275.76, 71.15) * mm, "end": v(-245.28, 71.15) * mm});
            skLineSegment(sketch, "E471", {"start": v(-245.28, 88.93) * mm, "end": v(-251.63, 88.93) * mm});
            skLineSegment(sketch, "E472", {"start": v(-251.63, 88.93) * mm, "end": v(-251.63, 82.58) * mm});
            skLineSegment(sketch, "E473", {"start": v(-251.63, 82.58) * mm, "end": v(-275.76, 82.58) * mm});
            skLineSegment(sketch, "E474", {"start": v(-275.76, 82.58) * mm, "end": v(-275.76, 95.28) * mm});
            skLineSegment(sketch, "E475", {"start": v(-199.56, 47.02) * mm, "end": v(-230.04, 47.02) * mm});
            skLineSegment(sketch, "E476", {"start": v(-230.04, 47.02) * mm, "end": v(-230.04, 64.8) * mm});
            skLineSegment(sketch, "E477", {"start": v(-230.04, 64.8) * mm, "end": v(-223.69, 64.8) * mm});
            skLineSegment(sketch, "E478", {"start": v(-223.69, 64.8) * mm, "end": v(-223.69, 58.45) * mm});
            skLineSegment(sketch, "E479", {"start": v(-223.69, 58.45) * mm, "end": v(-199.56, 58.45) * mm});
            skLineSegment(sketch, "E480", {"start": v(-199.56, 58.45) * mm, "end": v(-199.56, 71.15) * mm});
            skLineSegment(sketch, "E481", {"start": v(-199.56, 71.15) * mm, "end": v(-230.04, 71.15) * mm});
            skLineSegment(sketch, "E482", {"start": v(-230.04, 71.15) * mm, "end": v(-230.04, 88.93) * mm});
            skLineSegment(sketch, "E483", {"start": v(-230.04, 88.93) * mm, "end": v(-223.69, 88.93) * mm});
            skLineSegment(sketch, "E484", {"start": v(-223.69, 88.93) * mm, "end": v(-223.69, 82.58) * mm});
            skLineSegment(sketch, "E485", {"start": v(-223.69, 82.58) * mm, "end": v(-199.56, 82.58) * mm});
            skLineSegment(sketch, "E486", {"start": v(-199.56, 82.58) * mm, "end": v(-199.56, 95.28) * mm});
            skLineSegment(sketch, "E487", {"start": v(-245.28, 71.15) * mm, "end": v(-245.28, 88.93) * mm});
            skLineSegment(sketch, "E488", {"start": v(-275.76, 95.28) * mm, "end": v(-199.56, 95.28) * mm});
            skPoint(sketch, "E489", {"position": v(-237.66, 95.28) * mm});
            skLineSegment(sketch, "E490", {"start": v(-186.86, 47.02) * mm, "end": v(-156.38, 47.02) * mm});
            skLineSegment(sketch, "E491", {"start": v(-156.38, 47.02) * mm, "end": v(-156.38, 64.8) * mm});
            skLineSegment(sketch, "E492", {"start": v(-156.38, 64.8) * mm, "end": v(-162.73, 64.8) * mm});
            skLineSegment(sketch, "E493", {"start": v(-162.73, 64.8) * mm, "end": v(-162.73, 58.45) * mm});
            skLineSegment(sketch, "E494", {"start": v(-162.73, 58.45) * mm, "end": v(-186.86, 58.45) * mm});
            skLineSegment(sketch, "E495", {"start": v(-186.86, 58.45) * mm, "end": v(-186.86, 71.15) * mm});
            skLineSegment(sketch, "E496", {"start": v(-186.86, 71.15) * mm, "end": v(-156.38, 71.15) * mm});
            skLineSegment(sketch, "E497", {"start": v(-156.38, 88.93) * mm, "end": v(-162.73, 88.93) * mm});
            skLineSegment(sketch, "E498", {"start": v(-162.73, 88.93) * mm, "end": v(-162.73, 82.58) * mm});
            skLineSegment(sketch, "E499", {"start": v(-162.73, 82.58) * mm, "end": v(-186.86, 82.58) * mm});
            skLineSegment(sketch, "E500", {"start": v(-186.86, 82.58) * mm, "end": v(-186.86, 95.28) * mm});
            skLineSegment(sketch, "E501", {"start": v(-110.66, 47.02) * mm, "end": v(-141.14, 47.02) * mm});
            skLineSegment(sketch, "E502", {"start": v(-141.14, 47.02) * mm, "end": v(-141.14, 64.8) * mm});
            skLineSegment(sketch, "E503", {"start": v(-141.14, 64.8) * mm, "end": v(-134.79, 64.8) * mm});
            skLineSegment(sketch, "E504", {"start": v(-134.79, 64.8) * mm, "end": v(-134.79, 58.45) * mm});
            skLineSegment(sketch, "E505", {"start": v(-134.79, 58.45) * mm, "end": v(-110.66, 58.45) * mm});
            skLineSegment(sketch, "E506", {"start": v(-110.66, 58.45) * mm, "end": v(-110.66, 71.15) * mm});
            skLineSegment(sketch, "E507", {"start": v(-110.66, 71.15) * mm, "end": v(-141.14, 71.15) * mm});
            skLineSegment(sketch, "E508", {"start": v(-141.14, 71.15) * mm, "end": v(-141.14, 88.93) * mm});
            skLineSegment(sketch, "E509", {"start": v(-141.14, 88.93) * mm, "end": v(-134.79, 88.93) * mm});
            skLineSegment(sketch, "E510", {"start": v(-134.79, 88.93) * mm, "end": v(-134.79, 82.58) * mm});
            skLineSegment(sketch, "E511", {"start": v(-134.79, 82.58) * mm, "end": v(-110.66, 82.58) * mm});
            skLineSegment(sketch, "E512", {"start": v(-110.66, 82.58) * mm, "end": v(-110.66, 95.28) * mm});
            skLineSegment(sketch, "E513", {"start": v(-156.38, 71.15) * mm, "end": v(-156.38, 88.93) * mm});
            skLineSegment(sketch, "E514", {"start": v(-186.86, 95.28) * mm, "end": v(-110.66, 95.28) * mm});
            skPoint(sketch, "E515", {"position": v(-148.76, 95.28) * mm});
            skLineSegment(sketch, "E516", {"start": v(-97.96, 47.02) * mm, "end": v(-67.48, 47.02) * mm});
            skLineSegment(sketch, "E517", {"start": v(-67.48, 47.02) * mm, "end": v(-67.48, 64.8) * mm});
            skLineSegment(sketch, "E518", {"start": v(-67.48, 64.8) * mm, "end": v(-73.83, 64.8) * mm});
            skLineSegment(sketch, "E519", {"start": v(-73.83, 64.8) * mm, "end": v(-73.83, 58.45) * mm});
            skLineSegment(sketch, "E520", {"start": v(-73.83, 58.45) * mm, "end": v(-97.96, 58.45) * mm});
            skLineSegment(sketch, "E521", {"start": v(-97.96, 58.45) * mm, "end": v(-97.96, 71.15) * mm});
            skLineSegment(sketch, "E522", {"start": v(-97.96, 71.15) * mm, "end": v(-67.48, 71.15) * mm});
            skLineSegment(sketch, "E523", {"start": v(-67.48, 88.93) * mm, "end": v(-73.83, 88.93) * mm});
            skLineSegment(sketch, "E524", {"start": v(-73.83, 88.93) * mm, "end": v(-73.83, 82.58) * mm});
            skLineSegment(sketch, "E525", {"start": v(-73.83, 82.58) * mm, "end": v(-97.96, 82.58) * mm});
            skLineSegment(sketch, "E526", {"start": v(-97.96, 82.58) * mm, "end": v(-97.96, 95.28) * mm});
            skLineSegment(sketch, "E527", {"start": v(-21.76, 47.02) * mm, "end": v(-52.24, 47.02) * mm});
            skLineSegment(sketch, "E528", {"start": v(-52.24, 47.02) * mm, "end": v(-52.24, 64.8) * mm});
            skLineSegment(sketch, "E529", {"start": v(-52.24, 64.8) * mm, "end": v(-45.89, 64.8) * mm});
            skLineSegment(sketch, "E530", {"start": v(-45.89, 64.8) * mm, "end": v(-45.89, 58.45) * mm});
            skLineSegment(sketch, "E531", {"start": v(-45.89, 58.45) * mm, "end": v(-21.76, 58.45) * mm});
            skLineSegment(sketch, "E532", {"start": v(-21.76, 58.45) * mm, "end": v(-21.76, 71.15) * mm});
            skLineSegment(sketch, "E533", {"start": v(-21.76, 71.15) * mm, "end": v(-52.24, 71.15) * mm});
            skLineSegment(sketch, "E534", {"start": v(-52.24, 71.15) * mm, "end": v(-52.24, 88.93) * mm});
            skLineSegment(sketch, "E535", {"start": v(-52.24, 88.93) * mm, "end": v(-45.89, 88.93) * mm});
            skLineSegment(sketch, "E536", {"start": v(-45.89, 88.93) * mm, "end": v(-45.89, 82.58) * mm});
            skLineSegment(sketch, "E537", {"start": v(-45.89, 82.58) * mm, "end": v(-21.76, 82.58) * mm});
            skLineSegment(sketch, "E538", {"start": v(-21.76, 82.58) * mm, "end": v(-21.76, 95.28) * mm});
            skLineSegment(sketch, "E539", {"start": v(-67.48, 71.15) * mm, "end": v(-67.48, 88.93) * mm});
            skLineSegment(sketch, "E540", {"start": v(-97.96, 95.28) * mm, "end": v(-21.76, 95.28) * mm});
            skPoint(sketch, "E541", {"position": v(-59.86, 95.28) * mm});
            skPoint(sketch, "E542", {"position": v(-282.1, 95.28) * mm});
            skSolve(sketch);
        }
        {
            var Q0;
            Q0=makeQuery(id+"F0.imprint","IMPRINT",FACE,{"disambiguationData":[TD([[makeQuery(id+"F0.imprint","IMPRINT",EDGE,{"derivedFrom":sQuery(id+"F0.wireOp",EDGE,"E0")}),1.0]])]});
            extrude(context, id + "F1", {"entities" : qUnion([Q0]), "depth" : 6.35 * mm});
        }
    });
